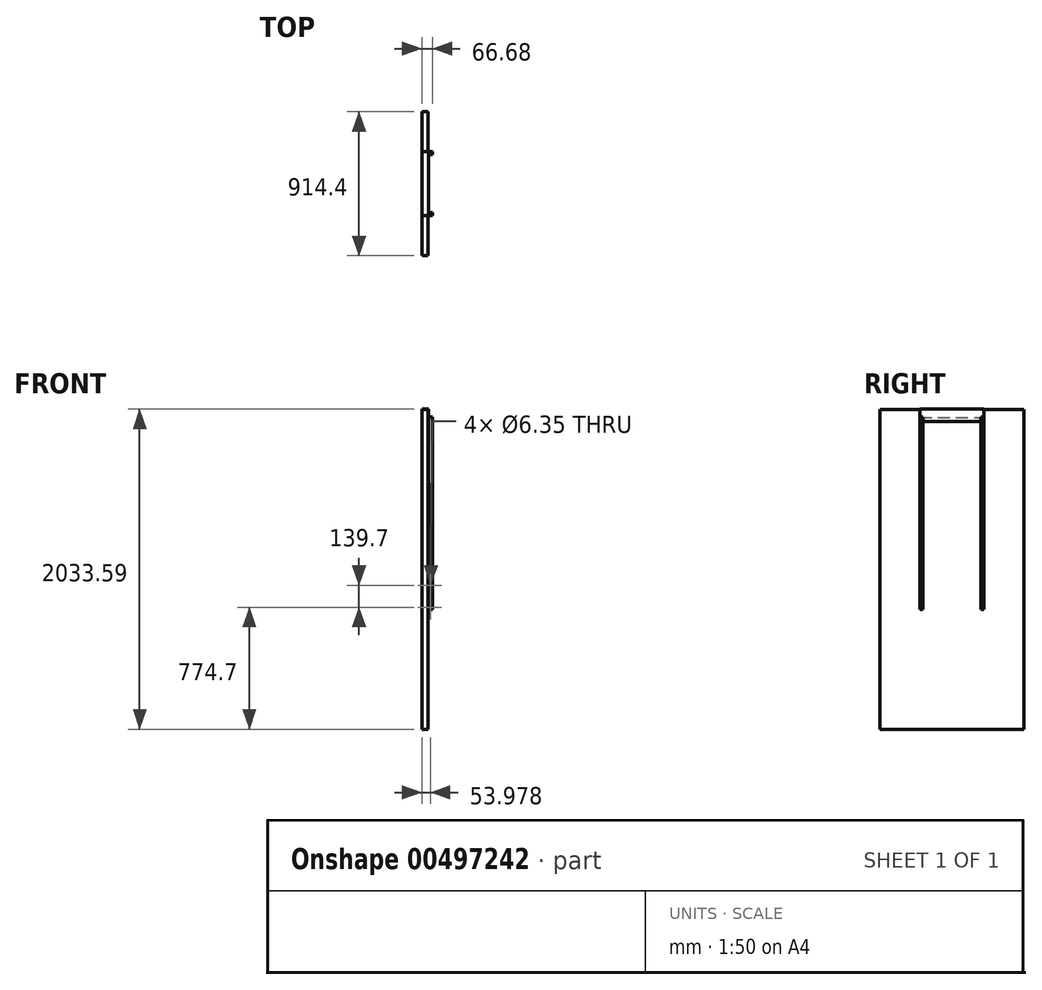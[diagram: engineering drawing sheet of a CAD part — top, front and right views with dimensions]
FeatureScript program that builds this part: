
annotation { "Feature Type Name" : "Feature", "Feature Type Description" : "" }
export const myFeature = defineFeature(function(context is Context, id is Id, definition is map)
    precondition{}
    {
        {
            var Q0;
            Q0=qCreatedBy(makeId("Right.planeOp"),FACE);
            var sketch = newSketch(context, id + "F0", { "sketchPlane" : qUnion([Q0])});
            skLineSegment(sketch, "E0.bottom", {"start": v(457.2, 0) * mm, "end": v(-457.2, 0) * mm});
            skLineSegment(sketch, "E0.top", {"start": v(457.2, 2032) * mm, "end": v(-457.2, 2032) * mm});
            skLineSegment(sketch, "E0.left", {"start": v(457.2, 0) * mm, "end": v(457.2, 2032) * mm});
            skLineSegment(sketch, "E0.right", {"start": v(-457.2, 0) * mm, "end": v(-457.2, 2032) * mm});
            skPoint(sketch, "E0.middle", {"position": v(0, 1016) * mm});
            skSolve(sketch);
        }
        {
            var Q0;
            Q0 = qSketchRegion(id + "F0", true);
            extrude(context, id + "F1", {"entities" : qUnion([Q0]), "depth" : 38.1 * mm});
        }
        {
            var Q0;
            Q0=qCreatedBy(makeId("Front.planeOp"),FACE);
            var sketch = newSketch(context, id + "F2", { "sketchPlane" : qUnion([Q0])});
            skLineSegment(sketch, "E1.0", {"start": v(0, 0) * mm, "end": v(0, 2032) * mm, "construction": true});
            skLineSegment(sketch, "E2.0", {"start": v(38.1, 0) * mm, "end": v(38.1, 2032) * mm, "construction": true});
            skLineSegment(sketch, "E3.0", {"start": v(38.1, 2032) * mm, "end": v(0, 2032) * mm, "construction": true});
            skLineSegment(sketch, "E4", {"start": v(0, 1981.2) * mm, "end": v(0, 2032) * mm});
            skLineSegment(sketch, "E5", {"start": v(38.1, 2032) * mm, "end": v(0, 2032) * mm});
            skLineSegment(sketch, "E6", {"start": v(38.1, 2032) * mm, "end": v(38.1, 1955.8) * mm});
            skLineSegment(sketch, "E7.0", {"start": v(39.69, 2033.59) * mm, "end": v(39.69, 1955.8) * mm});
            skLineSegment(sketch, "E7.1", {"start": v(39.69, 2033.59) * mm, "end": v(-1.59, 2033.59) * mm});
            skLineSegment(sketch, "E7.2", {"start": v(-1.59, 1981.2) * mm, "end": v(-1.59, 2033.59) * mm});
            skLineSegment(sketch, "E8", {"start": v(0, 1981.2) * mm, "end": v(-1.59, 1981.2) * mm});
            skLineSegment(sketch, "E9", {"start": v(39.69, 1955.8) * mm, "end": v(38.1, 1955.8) * mm});
            skSolve(sketch);
        }
        {
            var Q0;
            Q0 = qSketchRegion(id + "F2", true);
            extrude(context, id + "F3", {"entities" : qUnion([Q0]), "depth" : 406.4 * mm, "symmetric" : true});
        }
        {
            var Q0;
            Q0=makeQuery(id+"F3.opExtrude","SWEPT_FACE",FACE,{"disambiguationData":[OSD([sQuery(id+"F2.wireOp",EDGE,"E7.0")])]});
            var sketch = newSketch(context, id + "F4", { "sketchPlane" : qUnion([Q0])});
            skLineSegment(sketch, "E10", {"start": v(-203.2, 1982.79) * mm, "end": v(203.2, 1982.79) * mm, "construction": true});
            skLineSegment(sketch, "E11.bottom", {"start": v(-203.2, 1982.79) * mm, "end": v(-184.15, 1982.79) * mm});
            skLineSegment(sketch, "E11.top", {"start": v(-203.2, 762) * mm, "end": v(-184.15, 762) * mm});
            skLineSegment(sketch, "E11.left", {"start": v(-203.2, 1982.79) * mm, "end": v(-203.2, 762) * mm});
            skLineSegment(sketch, "E11.right", {"start": v(-184.15, 1982.79) * mm, "end": v(-184.15, 762) * mm});
            skLineSegment(sketch, "E12", {"start": v(0, 1982.79) * mm, "end": v(0, 2134.1) * mm, "construction": true});
            skPoint(sketch, "E12.endSnap0", {"position": v(0, 2033.59) * mm});
            skLineSegment(sketch, "E13", {"start": v(-203.2, 914.4) * mm, "end": v(-184.15, 914.4) * mm, "construction": true});
            skLineSegment(sketch, "E14.MirrorCS", {"start": v(184.15, 1982.79) * mm, "end": v(184.15, 762) * mm});
            skLineSegment(sketch, "E15.MirrorCS", {"start": v(203.2, 1982.79) * mm, "end": v(203.2, 762) * mm});
            skLineSegment(sketch, "E16.MirrorCS", {"start": v(203.2, 1982.79) * mm, "end": v(184.15, 1982.79) * mm});
            skLineSegment(sketch, "E17.MirrorCS", {"start": v(203.2, 762) * mm, "end": v(184.15, 762) * mm});
            skSolve(sketch);
        }
        {
            var Q0;
            Q0 = qSketchRegion(id + "F4", true);
            extrude(context, id + "F5", {"entities" : qUnion([Q0]), "depth" : 25.4 * mm});
        }
        {
            var Q0;
            Q0=makeQuery(id+"F5.opExtrude","SWEPT_FACE",FACE,{"disambiguationData":[OSD([sQuery(id+"F4.wireOp",EDGE,"E11.left")])]});
            var sketch = newSketch(context, id + "F6", { "sketchPlane" : qUnion([Q0])});
            skLineSegment(sketch, "E18", {"start": v(52.39, 762) * mm, "end": v(52.39, 914.4) * mm, "construction": true});
            skCircle(sketch, "E19", {"center": v(52.39, 914.4) * mm, "radius": 3.18 * mm});
            skCircle(sketch, "E20", {"center": v(52.39, 774.7) * mm, "radius": 3.18 * mm});
            skSolve(sketch);
        }
        {
            var Q0;
            Q0 = qSketchRegion(id + "F6", true);
            extrude(context, id + "F7", {"entities" : qUnion([Q0]), "operationType" : NewBodyOperationType.REMOVE, "endBound" : BoundingType.THROUGH_ALL, "oppositeDirection" : true, "depth" : 25.4 * mm});
        }
    });
